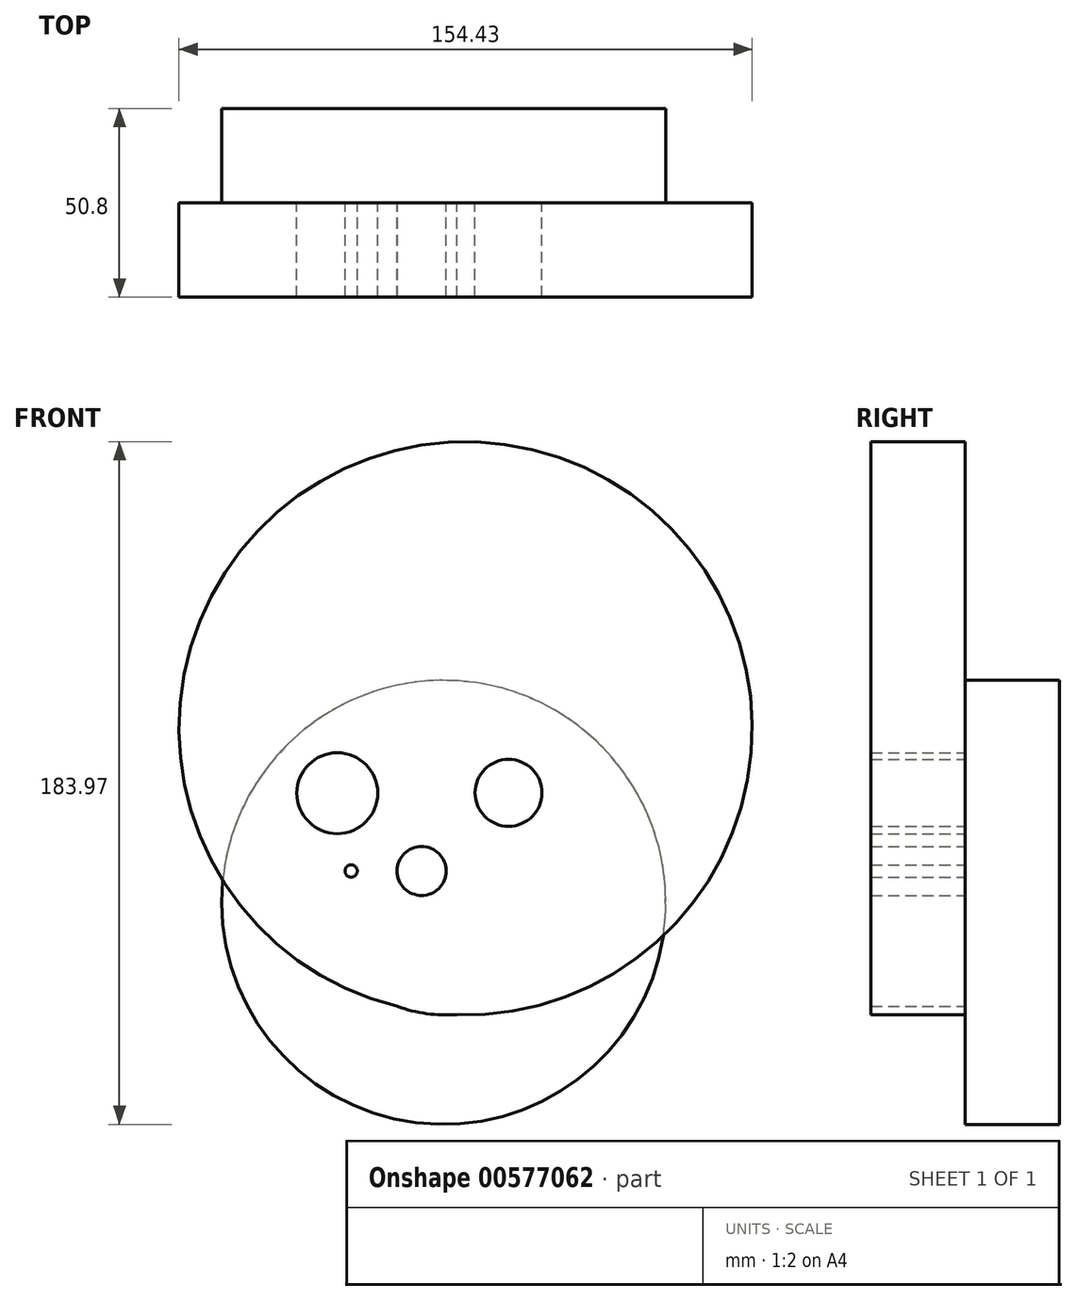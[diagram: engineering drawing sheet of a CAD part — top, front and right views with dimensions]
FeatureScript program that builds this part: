
annotation { "Feature Type Name" : "Feature", "Feature Type Description" : "" }
export const myFeature = defineFeature(function(context is Context, id is Id, definition is map)
    precondition{}
    {
        {
            var Q0;
            Q0=qCreatedBy(makeId("Front.planeOp"),FACE);
            var sketch = newSketch(context, id + "F0", { "sketchPlane" : qUnion([Q0])});
            skCircle(sketch, "E0", {"center": v(-51.36, 48.6) * mm, "radius": 59.84 * mm});
            skSolve(sketch);
        }
        {
            var Q0;
            Q0=makeQuery(id+"F0.imprint","IMPRINT",FACE,{"disambiguationData":[TD([[makeQuery(id+"F0.imprint","IMPRINT",EDGE,{"derivedFrom":sQuery(id+"F0.wireOp",EDGE,"E0")}),1.0]])]});
            extrude(context, id + "F1", {"entities" : qUnion([Q0]), "depth" : 25.4 * mm, "offsetDistance" : 25.4 * mm});
        }
        {
            var Q0;
            Q0=makeQuery(id+"F1.opExtrude","CAP_FACE",FACE,{"disambiguationData":[OSD([sQuery(id+"F0.wireOp",EDGE,"E0")])],"isStart":false});
            var sketch = newSketch(context, id + "F2", { "sketchPlane" : qUnion([Q0])});
            skCircle(sketch, "E1", {"center": v(-80.02, 78.02) * mm, "radius": 10.9 * mm});
            skCircle(sketch, "E2", {"center": v(-33.9, 78.11) * mm, "radius": 9.01 * mm});
            skCircle(sketch, "E3", {"center": v(-76.3, 57.06) * mm, "radius": 1.66 * mm});
            skCircle(sketch, "E4", {"center": v(-57.3, 57.06) * mm, "radius": 6.6 * mm});
            skCircle(sketch, "E5", {"center": v(-50.7, 57.06) * mm, "radius": 38.82 * mm});
            skCircle(sketch, "E6", {"center": v(-45.45, 95.52) * mm, "radius": 77.21 * mm});
            skSolve(sketch);
        }
        {
            var Q0;
            Q0 = qSketchRegion(id + "F2", true);
            extrude(context, id + "F3", {"entities" : qUnion([Q0]), "operationType" : NewBodyOperationType.ADD, "depth" : 25.4 * mm, "offsetDistance" : 25.4 * mm});
        }
    });
